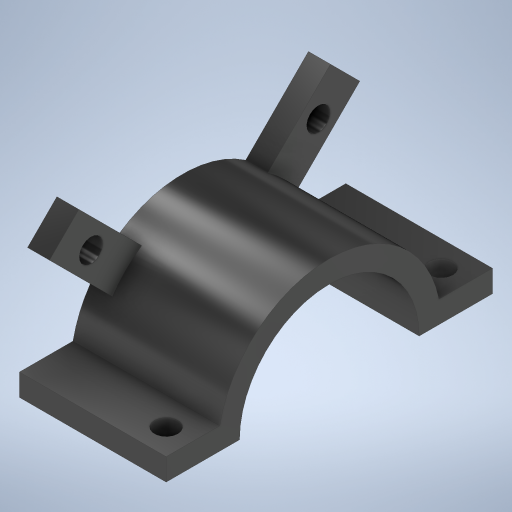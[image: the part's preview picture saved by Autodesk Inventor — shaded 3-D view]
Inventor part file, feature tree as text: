
AUTODESK INVENTOR PART (.ipt)
format: ipt  version: 2023 (Build 270158000, 158)  size: 315,904 bytes
history: native  units: mm
features: sketch x5, extrude x3, mirror x2, hole x2
ambient origin geometry x8: Origin, YZ Plane, XZ Plane, XY Plane, X Axis, Y Axis, Z Axis, Center Point
bodies: Volumenkörper1 (feature_tree)
feature tree (12):
  extrude  "Extrusion1"  Depth=15.25mm
  extrude  "Extrusion4"  Depth=20.0mm
  mirror  "Spiegeln4"
  hole  "Bohrung3"  [1 undecoded]
  extrude  "Extrusion5"  Depth=3.0mm TaperAngle=0.0deg
  hole  "Bohrung4"  [1 undecoded]
  mirror  "Spiegeln5"
  sketch  "Skizze1"  dims[d0=12.25mm d1=15.25mm]
  sketch  "Skizze7"  dims[d2=20.0mm d3=0.0mm d40=12.097mm]
  sketch  "Skizze8"  dims[d41=135.0deg d42=8.596mm]
  sketch  "Skizze9"  dims[d43=5.657mm d44=3.0mm d45=0.0mm]
  sketch  "Skizze10"  dims[d46=3.2mm d47=6.0mm d48=4.0mm d49=2.0mm d50=90.0deg d51=8.0mm d52=20.594885mm d53=5.162mm d54=5.162mm d55=2.8285mm d56=2.8285mm d57=7.0mm d58=3.0mm d59=20.0mm d60=0.0mm d61=3.2mm d62=6.0mm d63=4.0mm d64=2.0mm d65=90.0deg d66=8.0mm d67=20.594885mm d68=3.5mm d69=3.5mm]
note: 2 required parameter values undecoded (feature->parameter linkage not recoverable at this tier; creation-order binding heuristic only, values carry confidence <= 0.55)
